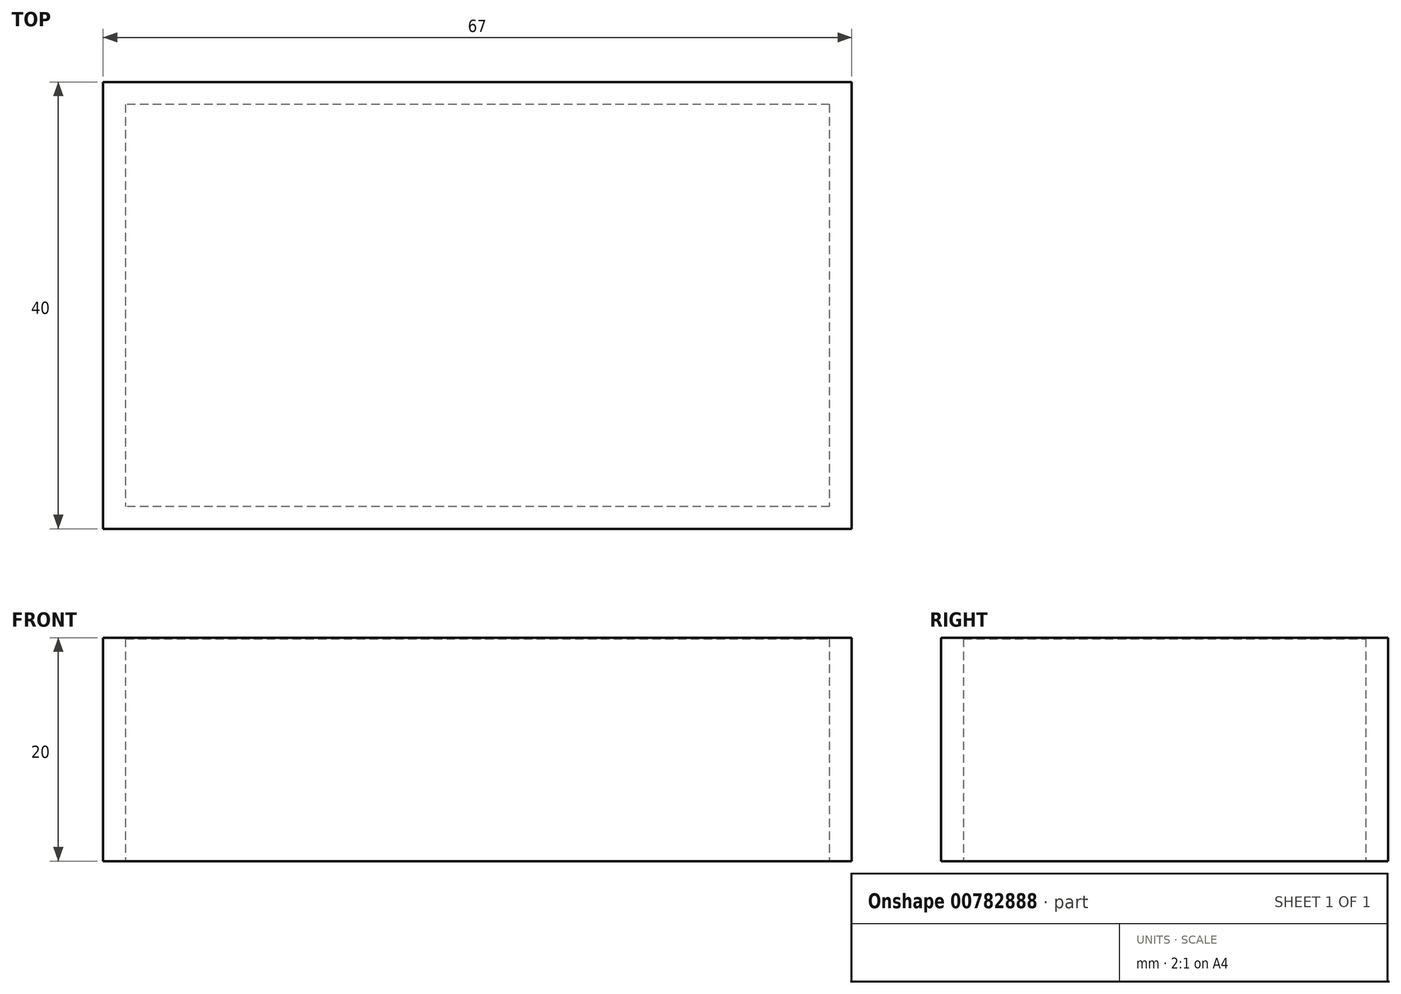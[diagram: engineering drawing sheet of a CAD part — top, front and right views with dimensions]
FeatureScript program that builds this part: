
annotation { "Feature Type Name" : "Feature", "Feature Type Description" : "" }
export const myFeature = defineFeature(function(context is Context, id is Id, definition is map)
    precondition{}
    {
        {
            var Q0;
            Q0=qCreatedBy(makeId("Front.planeOp"),FACE);
            var sketch = newSketch(context, id + "F0", { "sketchPlane" : qUnion([Q0])});
            skLineSegment(sketch, "E0.bottom", {"start": v(0, 0) * mm, "end": v(67, 0) * mm});
            skLineSegment(sketch, "E0.top", {"start": v(0, 57) * mm, "end": v(67, 57) * mm});
            skLineSegment(sketch, "E0.left", {"start": v(0, 0) * mm, "end": v(0, 57) * mm});
            skLineSegment(sketch, "E0.right", {"start": v(67, 0) * mm, "end": v(67, 57) * mm});
            skSolve(sketch);
        }
        {
            var Q0;
            Q0=makeQuery(id+"F0.imprint","IMPRINT",FACE,{"disambiguationData":[TD([[makeQuery(id+"F0.imprint","IMPRINT",EDGE,{"derivedFrom":sQuery(id+"F0.wireOp",EDGE,"E0.bottom")}),1.0]])]});
            extrude(context, id + "F1", {"entities" : qUnion([Q0]), "depth" : 40 * mm, "offsetDistance" : 25 * mm});
        }
        {
            var Q0;
            Q0=makeQuery(id+"F1.opExtrude","SWEPT_FACE",FACE,{"disambiguationData":[OSD([sQuery(id+"F0.wireOp",EDGE,"E0.bottom")])]});
            var sketch = newSketch(context, id + "F2", { "sketchPlane" : qUnion([Q0])});
            skLineSegment(sketch, "E1.0", {"start": v(2, 38) * mm, "end": v(65, 38) * mm});
            skLineSegment(sketch, "E1.1", {"start": v(2, 38) * mm, "end": v(2, 2) * mm});
            skLineSegment(sketch, "E1.2", {"start": v(2, 2) * mm, "end": v(65, 2) * mm});
            skLineSegment(sketch, "E1.3", {"start": v(65, 38) * mm, "end": v(65, 2) * mm});
            skSolve(sketch);
        }
        {
            var Q0;
            Q0 = qSketchRegion(id + "F2", true);
            extrude(context, id + "F3", {"entities" : qUnion([Q0]), "operationType" : NewBodyOperationType.REMOVE, "oppositeDirection" : true, "depth" : 55 * mm, "offsetDistance" : 25 * mm});
        }
        {
            var Q0;
            Q0 = qSketchRegion(id + "F2", true);
            extrude(context, id + "F4", {"entities" : qUnion([Q0]), "operationType" : NewBodyOperationType.REMOVE, "oppositeDirection" : true, "depth" : 56.9 * mm, "offsetDistance" : 25 * mm});
        }
        {
            var Q0;
            Q0=makeQuery(id+"F1.opExtrude","SWEPT_FACE",FACE,{"disambiguationData":[OSD([sQuery(id+"F0.wireOp",EDGE,"E0.bottom")])]});
            var sketch = newSketch(context, id + "F5", { "sketchPlane" : qUnion([Q0])});
            skLineSegment(sketch, "E2.bottom", {"start": v(106.32, -26.69) * mm, "end": v(-34.97, -26.69) * mm});
            skLineSegment(sketch, "E2.top", {"start": v(106.32, 67.78) * mm, "end": v(-34.97, 67.78) * mm});
            skLineSegment(sketch, "E2.left", {"start": v(106.32, -26.69) * mm, "end": v(106.32, 67.78) * mm});
            skLineSegment(sketch, "E2.right", {"start": v(-34.97, -26.69) * mm, "end": v(-34.97, 67.78) * mm});
            skSolve(sketch);
        }
        {
            var Q0;
            Q0 = qSketchRegion(id + "F5", true);
            extrude(context, id + "F6", {"entities" : qUnion([Q0]), "operationType" : NewBodyOperationType.REMOVE, "oppositeDirection" : true, "depth" : 20 * mm, "offsetDistance" : 25 * mm});
        }
        {
            var Q0;
            Q0=makeQuery(id+"F6.boolean.opBoolean","COPY",FACE,{"derivedFrom":makeQuery(id+"F6.opExtrude","CAP_FACE",FACE,{"disambiguationData":[OSD([sQuery(id+"F5.wireOp",EDGE,"E2.bottom"),sQuery(id+"F5.wireOp",EDGE,"E2.top"),sQuery(id+"F5.wireOp",EDGE,"E2.left"),sQuery(id+"F5.wireOp",EDGE,"E2.right")])],"isStart":false})});
            var sketch = newSketch(context, id + "F7", { "sketchPlane" : qUnion([Q0])});
            skLineSegment(sketch, "E3.bottom", {"start": v(122.93, -22.06) * mm, "end": v(-31.7, -22.06) * mm});
            skLineSegment(sketch, "E3.top", {"start": v(122.93, 56.62) * mm, "end": v(-31.7, 56.62) * mm});
            skLineSegment(sketch, "E3.left", {"start": v(122.93, -22.06) * mm, "end": v(122.93, 56.62) * mm});
            skLineSegment(sketch, "E3.right", {"start": v(-31.7, -22.06) * mm, "end": v(-31.7, 56.62) * mm});
            skSolve(sketch);
        }
        {
            var Q0;
            Q0 = qSketchRegion(id + "F7", true);
            extrude(context, id + "F8", {"entities" : qUnion([Q0]), "operationType" : NewBodyOperationType.REMOVE, "oppositeDirection" : true, "depth" : 17 * mm, "offsetDistance" : 25 * mm});
        }
    });
